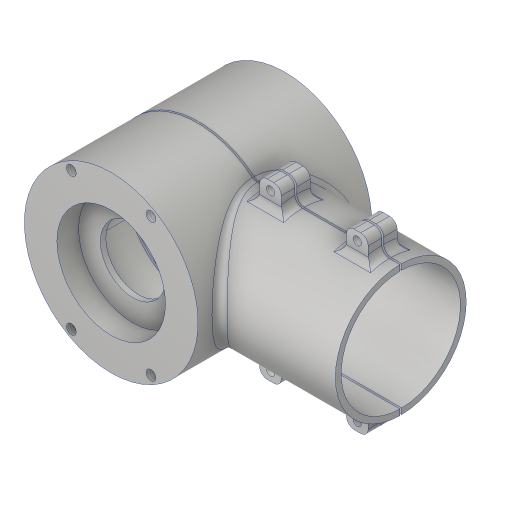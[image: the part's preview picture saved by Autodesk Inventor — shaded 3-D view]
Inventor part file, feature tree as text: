
AUTODESK INVENTOR PART (.ipt)
format: ipt  version: 2023.4 (Build 274418000, 418)  size: 797,184 bytes
history: native  units: in
note: dims shown in document units (in); Inventor stores cm internally (conversion verified against a paired STEP export)
features: sketch x25, extrude x16, projected_geometry x9, plane x8, hole x7, fillet x5, mirror x1, split x1
ambient origin geometry x8: Origin, YZ Plane, XZ Plane, XY Plane, X Axis, Y Axis, Z Axis, Center Point
bodies: Solid1 (feature_tree), Solid2 (feature_tree), Solid3 (feature_tree)
feature tree (72):
  extrude  "Extrusion1"  Depth=3.0in TaperAngle=0.0deg
  plane  "Work Plane1"
  extrude  "Extrusion2"  Depth=2.06in
  extrude  "Extrusion3"  Depth=3.0in TaperAngle=0.0deg
  hole  "Hole1"  [1 undecoded]
  plane  "Work Plane2"
  plane  "Work Plane3"
  extrude  "Extrusion5"  Depth=0.5in
  hole  "Hole2"  [1 undecoded]
  plane  "Work Plane8"
  extrude  "Extrusion14"  Depth=1.375in
  extrude  "Extrusion6"  Depth=0.13in
  hole  "Hole3"  [1 undecoded]
  fillet  "Fillet4"  Radius=1.0in
  mirror  "Mirror2"
  hole  "Hole5"  [1 undecoded]
  sketch  "Sketch14"  dims[d45=2.375in]
  plane  "Work Plane4"
  extrude  "Extrusion8"  Depth=1.5in
  fillet  "Fillet5"  Radius=0.5in
  plane  "Work Plane5"
  extrude  "Extrusion9"  Depth=1.5in TaperAngle=0.0deg
  plane  "Work Plane6"
  extrude  "Extrusion10"  Depth=0.375in
  fillet  "Fillet6"  Radius=0.5in
  hole  "Hole6"  [1 undecoded]
  plane  "Work Plane7"
  extrude  "Extrusion11"  Depth=1.5in
  split  "Split1"
  extrude  "Extrusion12"  [1 undecoded]
  extrude  "Extrusion13"  Depth=0.125in TaperAngle=0.0deg
  sketch  "Sketch23"  dims[d97=0.13in]
  extrude  "Extrusion15"  Depth=0.015in TaperAngle=0.0deg
  extrude  "Extrusion16"  Depth=0.125in
  fillet  "Fillet7"  Radius=0.125in
  extrude  "Extrusion17"  Depth=1.0in TaperAngle=0.0deg
  extrude  "Extrusion18"  TaperAngle=0.0deg  [1 undecoded]
  fillet  "Fillet8"  Radius=0.5in
  hole  "Hole10"  [1 undecoded]
  hole  "Hole11"  [1 undecoded]
  sketch  "Sketch1"  dims[d0=3.0in d1=3.0in d2=0.0in]
  sketch  "Sketch2"  dims[d3=3.5in d4=2.06in]
  sketch  "Sketch3"  dims[d5=0.1in d6=3.0in d7=0.0in]
  sketch  "Sketch4"  dims[d8=3.3in d9=0.0in]
  sketch  "Sketch7"  dims[d11=1.125in d12=0.75in d13=1.875in d14=0.375in d15=0.5635in d16=1.625in d17=0.8108in d22=1.5in d27=-1.875in]
  sketch  "Sketch8"  dims[d28=0.375in d29=0.5in]
  sketch  "Sketch9"  dims[d30=1.0in d31=0.0in]
  sketch  "Sketch10"  dims[d34=1.125in d35=0.75in d36=1.875in d37=0.375in d38=0.5635in d39=1.0in d40=0.8108in d41=2.0625in d42=0.0in]
  sketch  "Sketch13"  dims[d43=2.744in d44=1.375in]
  sketch  "Sketch15"  dims[d46=0.171in d47=0.432in d48=0.385in d49=0.25in d50=0.5635in d51=1.0in d52=0.8108in d69=0.13in]
  sketch  "Sketch16"  dims[d70=0.156in d71=0.38in d72=0.375in d73=0.25in d74=0.5635in d75=1.0in d76=0.8108in d77=45.0deg d78=1.0in]
  sketch  "Sketch17"  dims[d79=1.0in d80=0.0in d81=0.02in]
  sketch  "Sketch18"  dims[d83=1.5in d84=0.375in d85=0.5in]
  sketch  "Sketch19"  dims[d86=1.5in d87=0.5in d88=0.0in]
  sketch  "Sketch20"  dims[d89=-1.5in d90=0.375in d91=0.5in]
  sketch  "Sketch21"  dims[d92=1.5in d93=0.5in d94=0.0in]
  sketch  "Sketch22"  dims[d95=1.5in d96=1.5in]
  sketch  "Sketch24"  dims[d98=0.145in d99=0.38in d100=0.385in d101=0.25in d102=0.5635in d103=1.0in d104=0.8108in d105=-2.0in]
  sketch  "Sketch26"  dims[d106=0.1in d107=0.125in d108=0.0in]
  sketch  "Sketch28"  dims[d109=0.015in d110=0.0in d111=0.015in d112=0.0in]
  sketch  "Sketch29"  dims[d113=-1.875in d114=0.125in d115=0.125in d116=0.0in]
  sketch  "Sketch30"  dims[d117=0.0in d118=0.0in d127=1.0in d128=0.0in]
  sketch  "Sketch31"  dims[d129=0.26in d144=0.0in d145=0.0in d146=0.5in d147=1.25in d148=0.5in d149=1.25in d150=1.0in d151=0.0in d152=0.26in d153=0.156in d154=0.5in d155=0.375in d156=0.25in d157=0.5635in d158=0.75in d159=0.8108in d160=0.201in d161=0.75in d162=0.375in d163=0.19in d164=0.5635in d165=1.0in d166=0.8108in]
  projected_geometry  "Project Cut Edges3"
  projected_geometry  "Project Cut Edges4"
  projected_geometry  "Project Cut Edges5"
  projected_geometry  "Project Cut Edges6"
  projected_geometry  "Project Cut Edges7"
  projected_geometry  "Project Cut Edges8"
  projected_geometry  "Project Cut Edges9"
  projected_geometry  "Project Cut Edges10"
  projected_geometry  "Project Cut Edges11"
note: 9 required parameter values undecoded (feature->parameter linkage not recoverable at this tier; creation-order binding heuristic only, values carry confidence <= 0.55)
